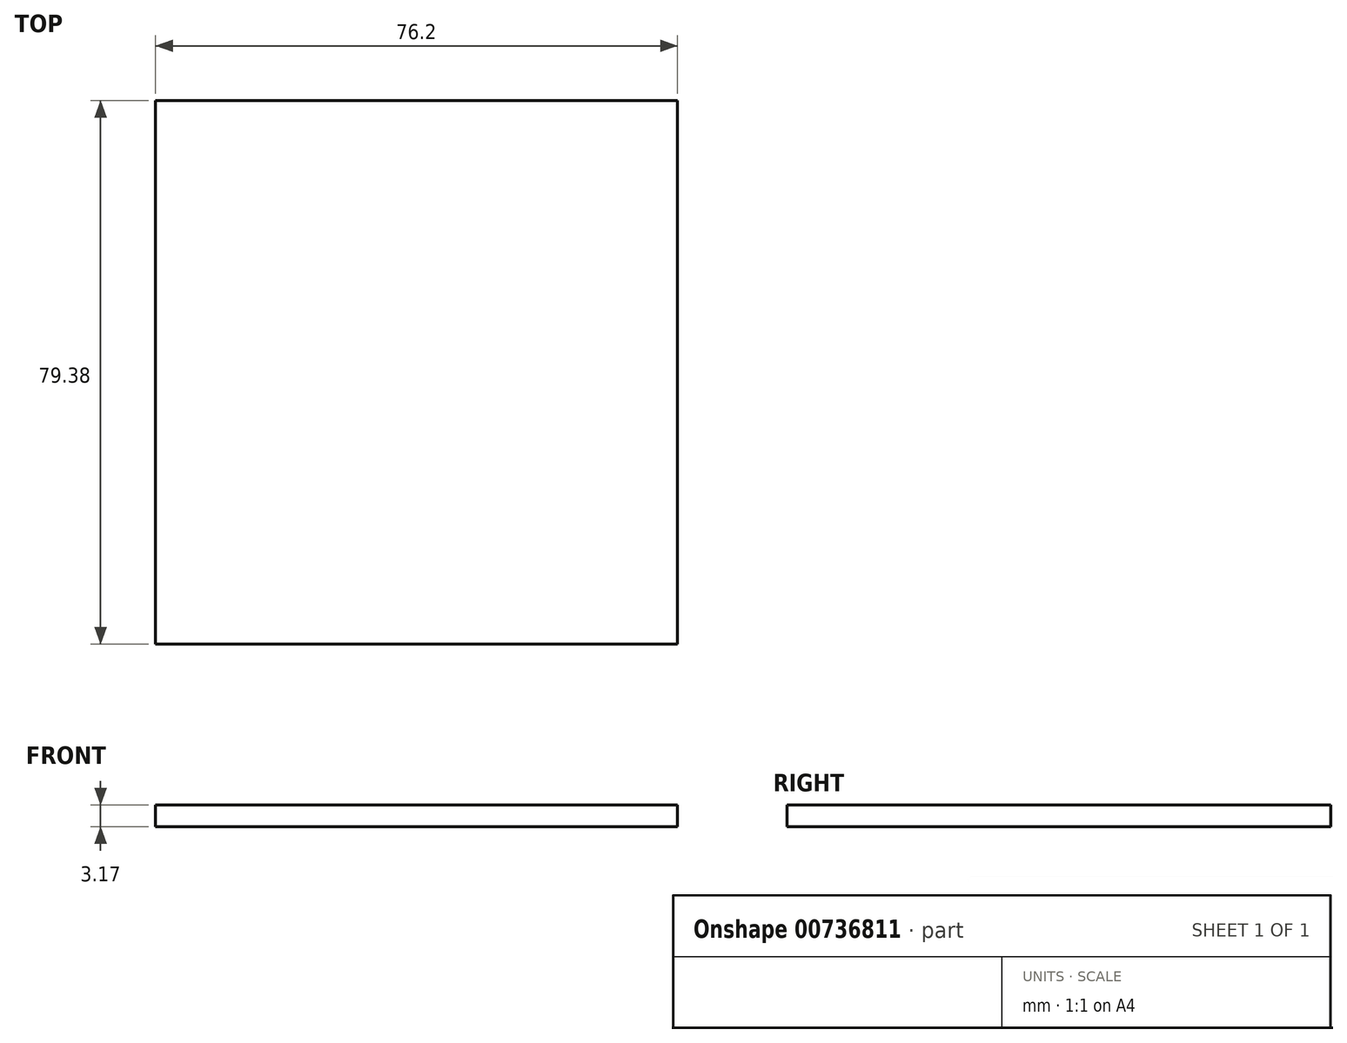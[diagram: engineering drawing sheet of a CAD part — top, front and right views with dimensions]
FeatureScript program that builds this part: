
annotation { "Feature Type Name" : "Feature", "Feature Type Description" : "" }
export const myFeature = defineFeature(function(context is Context, id is Id, definition is map)
    precondition{}
    {
        {
            var Q0;
            Q0=qCreatedBy(makeId("Top.planeOp"),FACE);
            var sketch = newSketch(context, id + "F0", { "sketchPlane" : qUnion([Q0])});
            skLineSegment(sketch, "E0.bottom", {"start": v(0, 0) * mm, "end": v(-76.2, 0) * mm});
            skLineSegment(sketch, "E0.top", {"start": v(0, 79.38) * mm, "end": v(-76.2, 79.38) * mm});
            skLineSegment(sketch, "E0.left", {"start": v(0, 0) * mm, "end": v(0, 79.37) * mm});
            skLineSegment(sketch, "E0.right", {"start": v(-76.2, 0) * mm, "end": v(-76.2, 79.38) * mm});
            skSolve(sketch);
        }
        {
            var Q0;
            Q0=makeQuery(id+"F0.imprint","IMPRINT",FACE,{"disambiguationData":[TD([[makeQuery(id+"F0.imprint","IMPRINT",EDGE,{"derivedFrom":sQuery(id+"F0.wireOp",EDGE,"E0.bottom")}),-1.0]])]});
            extrude(context, id + "F1", {"entities" : qUnion([Q0]), "depth" : 3.17 * mm, "offsetDistance" : 25.4 * mm});
        }
    });
